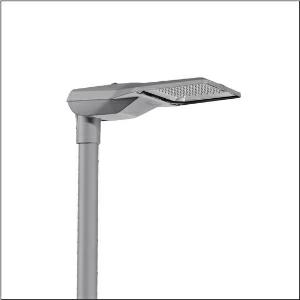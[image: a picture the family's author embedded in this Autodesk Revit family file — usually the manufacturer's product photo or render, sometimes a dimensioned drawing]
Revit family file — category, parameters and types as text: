
# Revit family: streetlight_sl_21_midi___st0_5a_5xe3b33s08lb_3b8c
name_source: partatom
category: Lighting Fixtures
units: mm (PartAtom-declared; Revit-internal decimal feet)

## family parameters
Cut with Voids When Loaded = No
Host = Face
Light Source = No
Part Type = Normal
Room Calculation Point = No
Round Connector Dimension = Use Diameter
Shared = No

## types (1)
- --- (1 x LED, 14340 lm, 98.3 W, 3000K)
    Apparent Load = 98 VA
    CIE Flux Codes = 41 75 97 100 100
    Color Rendering = 70
    Color Temperature = 3000K
    Default Elevation = 1800 mm
    Description = Streetlight SL 21 midi, mast luminaire, primary light control with lens, of PMMA, primary optical cover: cover, of toughened safety glass, transparent, light distribution: ST0.5a, light emission: direct distribution, primary light characteristic: asymmetric, installation type: side-entry, post-top, LED, High Power LED, rated luminous flux: 14.340lm, luminous efficacy: 146lm/W, light colour: 730, colour temperature: 3000K, control: overheat protection, constant luminous flux control, time-dependent luminous flux control, flexible luminous flux parameterisation, presetting dimming logarithmic, mains connection: 230..240V, AC, 50/60Hz, start of lifetime: 98W, end of service life: 101W, reduction: 45W, luminaire housing, of diecast aluminium, powder-coated, Siteco® metallic grey (DB 702S), corrosivity category C5 mid according to DIN EN ISO 12944, please order mast flange separately, inclination adjustable: 0°, 5°, 10°, 15°, sealing non-destructively replaceable, multi-level sealing system, length: 644mm, width: 335mm, height: 110mm, mast flange for spigot size: 42mm (side-entry): 5XC10008XM4, 60/48mm (side-entry/post-top): 5XC10108XM2, 76/60mm (side-entry/post-top): 5XC10108XM1, Smart Interface above, protection rating (complete): IP66, insulation class (complete): insulation class II (safety insulation), certification: CE, ENEC, ENEC+, VDE, impact resistance: IK09, permissible operating ambient temperature for outdoor applications: -40..+50°C, standard-compliant lighting for roads and squares, packaging unit: 1 piece

Light Distribution: ST0.5a
    Height = 111 mm
    Lamp = 1 x LED
    Lamp Light Flux = 14340 lm
    Lamp Power = 98.3 W
    Lamp count = 1
    Length = 644 mm
    Luminous efficacy = 146 lm/W
    Manufacturer = Siteco
    ModVariant = No
    Model = 5XE3B33S08LB
    Number of Poles = 1
    OnlyDefault = Yes
    Power Factor = 1
    Product Name = Streetlight SL 21 midi | ST0.5a
    Product group = mast luminaire | pylon top
    ProductGroupID = 6100
    Protection Class = Protection class II
    Protection Degree = IP 66
    RLX_Detail_Level = 1
    RLX_Emergency_Light_Flux = 0 lm
    RLX_Emergency_Type = 0
    RLX_Emergency_Type_DB = No
    RlxData = <blob elided: 101345 chars, md5=4f894141>
    Socket = socket
    Standby Power = 0 W
    System Light Flux = 14340 lm
    System Power = 98 W
    Type Comments = factory setting: luminous flux: 100 % | dim-lin: 254 | 1020 mA
    Type Image = l_1004302.jpg
    URL = http://relux.com
    VarID = @adj_126017
    Voltage = 0 V
    Weight = 0.00 kg
    Width = 336 mm

## geometry (parser evidence)
native form markers: Blend x4, Sweep x10
no freeform markers — native parametric forms only
